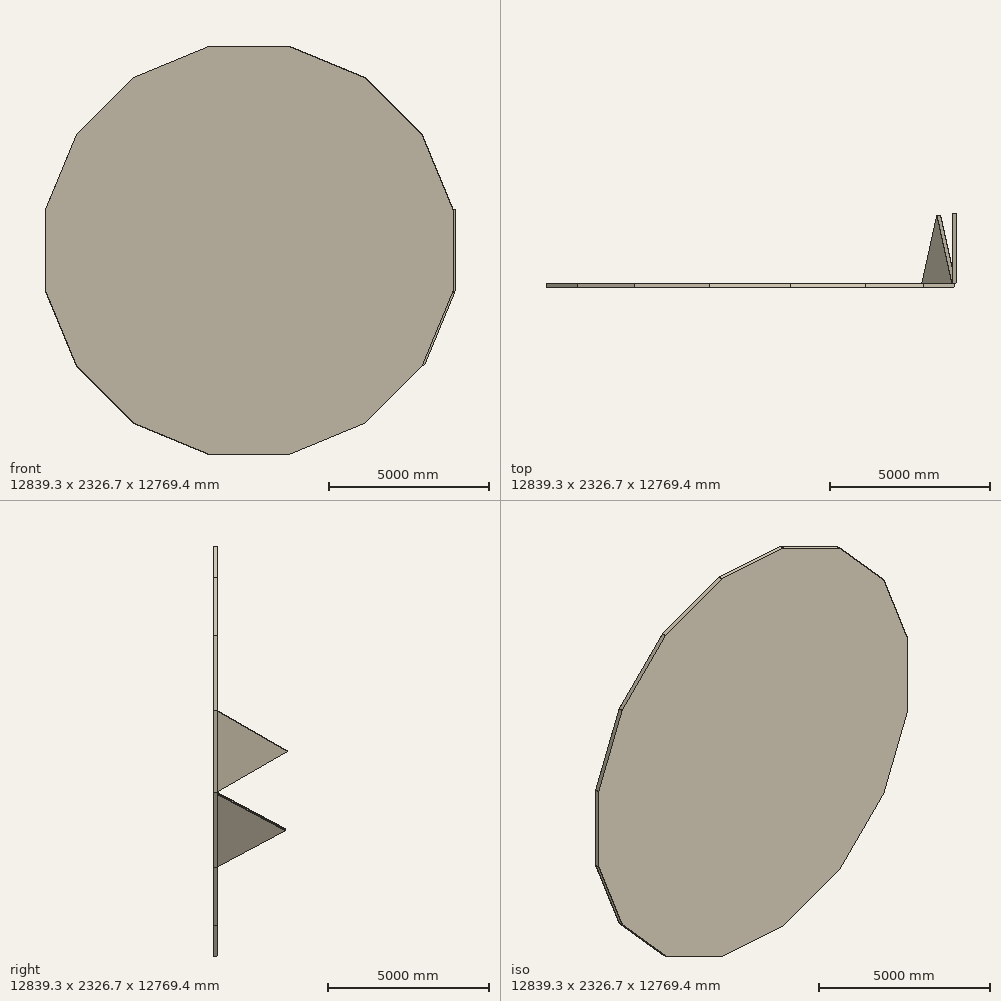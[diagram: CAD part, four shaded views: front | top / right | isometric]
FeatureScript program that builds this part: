
annotation { "Feature Type Name" : "Feature", "Feature Type Description" : "" }
export const myFeature = defineFeature(function(context is Context, id is Id, definition is map)
    precondition{}
    {
        {
            var Q0;
            Q0=qCreatedBy(makeId("Front.planeOp"),FACE);
            var sketch = newSketch(context, id + "F0", { "sketchPlane" : qUnion([Q0])});
            skCircle(sketch, "E0.cCircle", {"center": v(0, 0) * mm, "radius": 6384.72 * mm, "construction": true});
            skLineSegment(sketch, "E0.0", {"start": v(6384.72, 1270) * mm, "end": v(6384.72, -1270) * mm});
            skLineSegment(sketch, "E0.1", {"start": v(6384.72, -1270) * mm, "end": v(5412.7, -3616.65) * mm});
            skLineSegment(sketch, "E0.2", {"start": v(5412.7, -3616.65) * mm, "end": v(3616.65, -5412.7) * mm});
            skLineSegment(sketch, "E0.3", {"start": v(3616.65, -5412.7) * mm, "end": v(1270, -6384.72) * mm});
            skLineSegment(sketch, "E0.4", {"start": v(1270, -6384.72) * mm, "end": v(-1270, -6384.72) * mm});
            skLineSegment(sketch, "E0.5", {"start": v(-1270, -6384.72) * mm, "end": v(-3616.65, -5412.7) * mm});
            skLineSegment(sketch, "E0.6", {"start": v(-3616.65, -5412.7) * mm, "end": v(-5412.7, -3616.65) * mm});
            skLineSegment(sketch, "E0.7", {"start": v(-5412.7, -3616.65) * mm, "end": v(-6384.72, -1270) * mm});
            skLineSegment(sketch, "E0.8", {"start": v(-6384.72, -1270) * mm, "end": v(-6384.72, 1270) * mm});
            skLineSegment(sketch, "E0.9", {"start": v(-6384.72, 1270) * mm, "end": v(-5412.7, 3616.65) * mm});
            skLineSegment(sketch, "E0.10", {"start": v(-5412.7, 3616.65) * mm, "end": v(-3616.65, 5412.7) * mm});
            skLineSegment(sketch, "E0.11", {"start": v(-3616.65, 5412.7) * mm, "end": v(-1270, 6384.72) * mm});
            skLineSegment(sketch, "E0.12", {"start": v(-1270, 6384.72) * mm, "end": v(1270, 6384.72) * mm});
            skLineSegment(sketch, "E0.13", {"start": v(1270, 6384.72) * mm, "end": v(3616.65, 5412.7) * mm});
            skLineSegment(sketch, "E0.14", {"start": v(3616.65, 5412.7) * mm, "end": v(5412.7, 3616.65) * mm});
            skLineSegment(sketch, "E0.15", {"start": v(5412.7, 3616.65) * mm, "end": v(6384.72, 1270) * mm});
            skPoint(sketch, "E0.0.midPoint", {"position": v(6384.72, 0) * mm});
            skSolve(sketch);
        }
        {
            var Q0;
            Q0 = qSketchRegion(id + "F0", true);
            extrude(context, id + "F1", {"entities" : qUnion([Q0]), "endBound" : BoundingType.SYMMETRIC, "depth" : 127 * mm});
        }
        {
            var Q0;
            Q0=makeQuery(id+"F1.opExtrude","SWEPT_FACE",FACE,{"disambiguationData":[OSD([sQuery(id+"F0.wireOp",EDGE,"E0.1")])]});
            var sketch = newSketch(context, id + "F2", { "sketchPlane" : qUnion([Q0])});
            skCircle(sketch, "E1.cCircle", {"center": v(733.23, 0) * mm, "radius": 733.23 * mm, "construction": true});
            skLineSegment(sketch, "E1.0", {"start": v(0, -1270) * mm, "end": v(0, 1270) * mm});
            skLineSegment(sketch, "E1.1", {"start": v(0, 1270) * mm, "end": v(2199.7, 0) * mm});
            skLineSegment(sketch, "E1.2", {"start": v(2199.7, 0) * mm, "end": v(0, -1270) * mm});
            skPoint(sketch, "E1.0.midPoint", {"position": v(0, 0) * mm});
            skSolve(sketch);
        }
        {
            var Q0;
            {var subQ0=sQuery(id+"F2.wireOp",EDGE,"E1.2");var subQ1=sQuery(id+"F2.wireOp",EDGE,"E1.1");var subQ2=makeQuery(id+"F2.imprint","INTERSECT",VERTEX,{"derivedFrom":[subQ1,subQ0]});Q0=makeQuery(id+"F2.imprint","IMPRINT",FACE,{"disambiguationData":[TD([[makeQuery(id+"F2.imprint","IMPRINT",EDGE,{"disambiguationData":[TD([[subQ2,1.0]])],"derivedFrom":subQ1}),-1.0]])]});}
            extrude(context, id + "F3", {"entities" : qUnion([Q0]), "operationType" : NewBodyOperationType.ADD, "endBound" : BoundingType.SYMMETRIC, "depth" : 127 * mm});
        }
        {
            var Q0;
            Q0=makeQuery(id+"F1.opExtrude","SWEPT_FACE",FACE,{"disambiguationData":[OSD([sQuery(id+"F0.wireOp",EDGE,"E0.0")])]});
            cPlane(context, id + "F4", {"entities" : qUnion([Q0]), "cplaneType" : CPlaneType.OFFSET, "offset" : 6.35 * mm, "width" : 152.4 * mm, "height" : 152.4 * mm});
        }
        {
            var Q0;
            Q0=qCreatedBy(id+"F4.planeOp",FACE);
            var sketch = newSketch(context, id + "F5", { "sketchPlane" : qUnion([Q0])});
            skCircle(sketch, "E2.cCircle", {"center": v(796.73, 0) * mm, "radius": 733.23 * mm, "construction": true});
            skLineSegment(sketch, "E2.0", {"start": v(63.5, -1270) * mm, "end": v(63.5, 1270) * mm});
            skLineSegment(sketch, "E2.1", {"start": v(63.5, 1270) * mm, "end": v(2263.2, 0) * mm});
            skLineSegment(sketch, "E2.2", {"start": v(2263.2, 0) * mm, "end": v(63.5, -1270) * mm});
            skPoint(sketch, "E2.0.midPoint", {"position": v(63.5, 0) * mm});
            skLineSegment(sketch, "E3", {"start": v(2263.2, 0) * mm, "end": v(63.5, 0) * mm});
            skSolve(sketch);
        }
        {
            var Q0;
            Q0 = qSketchRegion(id + "F5", true);
            extrude(context, id + "F6", {"entities" : qUnion([Q0]), "operationType" : NewBodyOperationType.ADD, "endBound" : BoundingType.SYMMETRIC, "depth" : 127 * mm});
        }
        {
            var Q0;
            Q0=makeQuery(id+"F6.opExtrude","CAP_FACE",FACE,{"disambiguationData":[OSD([sQuery(id+"F5.wireOp",EDGE,"E2.0"),sQuery(id+"F5.wireOp",EDGE,"E2.1"),sQuery(id+"F5.wireOp",EDGE,"E2.2")])],"isStart":true});
            var sketch = newSketch(context, id + "F7", { "sketchPlane" : qUnion([Q0])});
            skSolve(sketch);
        }
        {
            var Q0;
            Q0=makeQuery(id+"F7.imprint","IMPRINT",FACE,{"disambiguationData":[TD([[makeQuery(id+"F7.imprint","IMPRINT",EDGE,{"derivedFrom":makeQuery(id+"F6.opExtrude","CAP_EDGE",EDGE,{"disambiguationData":[OSD([sQuery(id+"F5.wireOp",EDGE,"E2.1")])],"isStart":true})}),1.0]])]});
            cPlane(context, id + "F8", {"entities" : qUnion([Q0]), "cplaneType" : CPlaneType.OFFSET, "offset" : 167.64 * mm, "width" : 152.4 * mm, "height" : 152.4 * mm});
        }
        {
            var Q0;
            Q0=qCreatedBy(id+"F8.planeOp",FACE);
            var sketch = newSketch(context, id + "F9", { "sketchPlane" : qUnion([Q0])});
            skLineSegment(sketch, "E4", {"start": v(-2263.1, 0) * mm, "end": v(-63.52, 0) * mm});
            skSolve(sketch);
        }
        {
            var Q0;
            Q0=sQuery(id+"F5.wireOp",EDGE,"E3");
            var Q1;
            Q1=sQuery(id+"F9.wireOp",EDGE,"E4");
            cPlane(context, id + "F10", {"entities" : qUnion([Q0, Q1]), "cplaneType" : CPlaneType.LINE_ANGLE, "offset" : 25.4 * mm, "angle" : 0 * degree, "width" : 152.4 * mm, "height" : 152.4 * mm});
        }
    });
